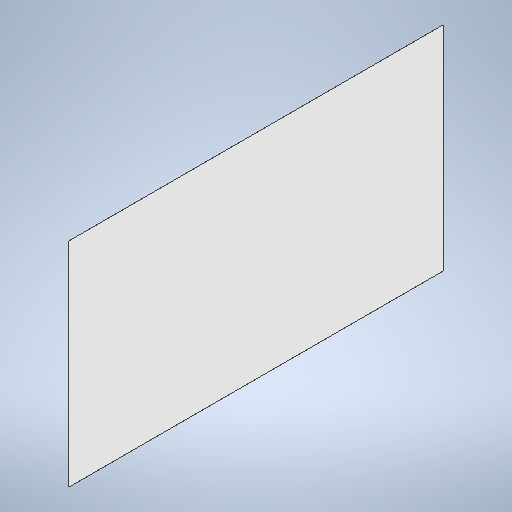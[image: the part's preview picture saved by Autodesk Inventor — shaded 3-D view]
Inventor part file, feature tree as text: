
AUTODESK INVENTOR PART (.ipt)
format: ipt  version: 2025 (Build 290162010, 162A)  size: 196,096 bytes
history: native  units: in
note: dims shown in document units (in); Inventor stores cm internally (conversion verified against a paired STEP export)
features: extrude x1, sketch x1
ambient origin geometry x8: Origin, YZ Plane, XZ Plane, XY Plane, X Axis, Y Axis, Z Axis, Center Point
bodies: Solid1 (feature_tree)
feature tree (2):
  extrude  "Extrusion1"  Depth=289.125in
  sketch  "Sketch1"  dims[d2=0.0625in d3=0.0in d4=289.125in d5=164.794in]
